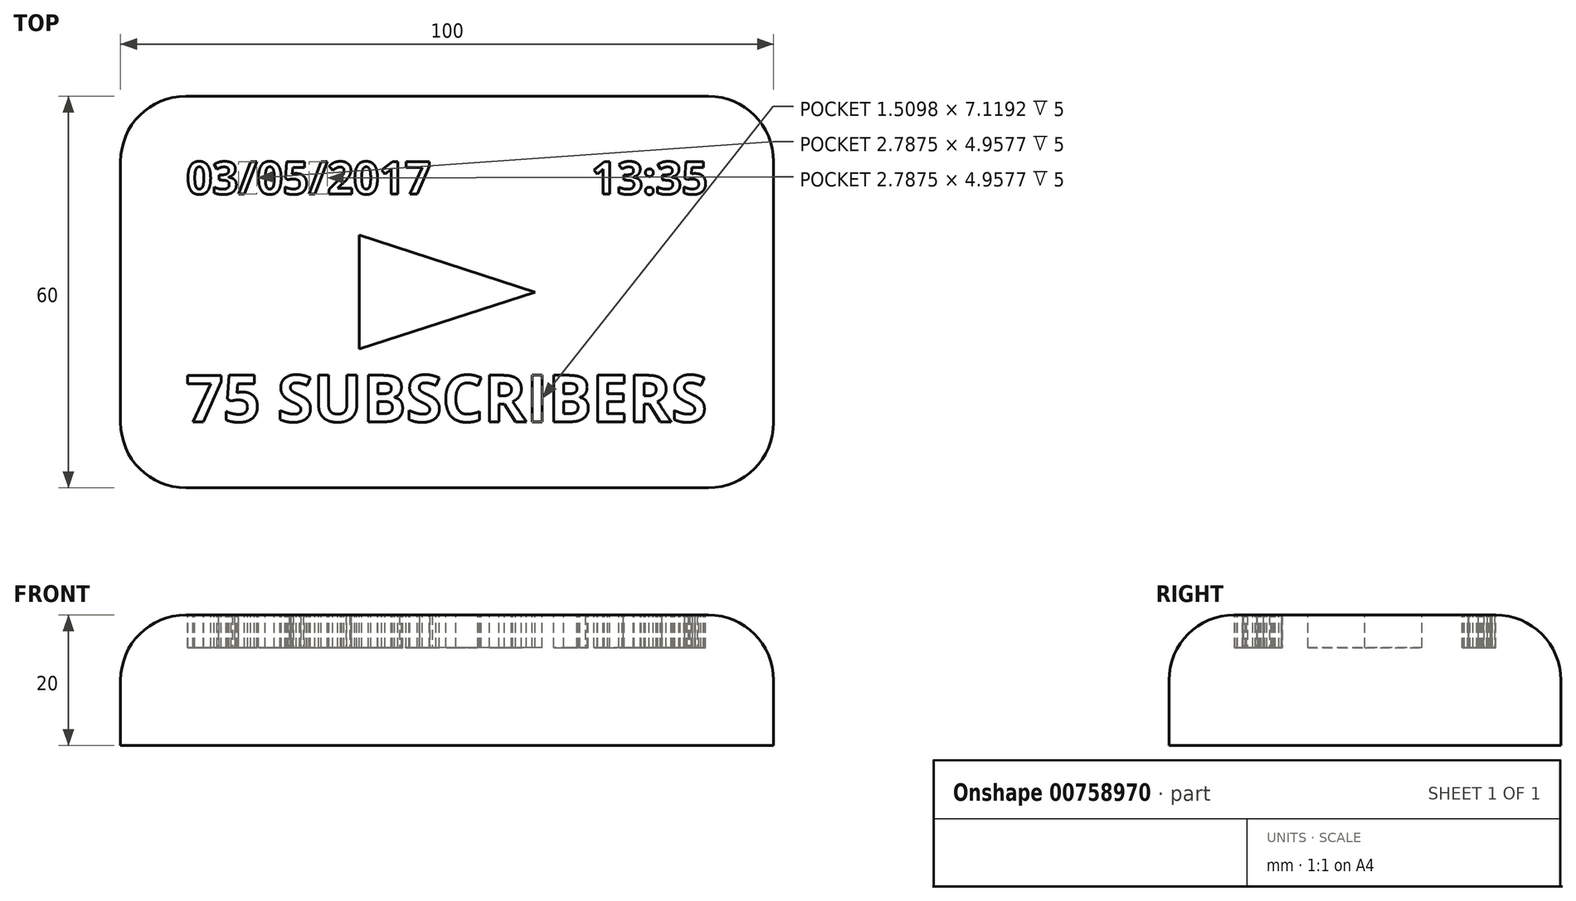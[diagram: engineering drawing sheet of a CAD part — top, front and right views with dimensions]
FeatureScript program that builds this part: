
annotation { "Feature Type Name" : "Feature", "Feature Type Description" : "" }
export const myFeature = defineFeature(function(context is Context, id is Id, definition is map)
    precondition{}
    {
        {
            var Q0;
            Q0=qCreatedBy(makeId("Top.planeOp"),FACE);
            var sketch = newSketch(context, id + "F0", { "sketchPlane" : qUnion([Q0])});
            skLineSegment(sketch, "E0.bottom", {"start": v(50, 30) * mm, "end": v(-50, 30) * mm});
            skLineSegment(sketch, "E0.top", {"start": v(50, -30) * mm, "end": v(-50, -30) * mm});
            skLineSegment(sketch, "E0.left", {"start": v(50, 30) * mm, "end": v(50, -30) * mm});
            skLineSegment(sketch, "E0.right", {"start": v(-50, 30) * mm, "end": v(-50, -30) * mm});
            skPoint(sketch, "E0.middle", {"position": v(0, 0) * mm});
            skSolve(sketch);
        }
        {
            var Q0;
            Q0=makeQuery(id+"F0.imprint","IMPRINT",FACE,{"disambiguationData":[TD([[makeQuery(id+"F0.imprint","IMPRINT",EDGE,{"derivedFrom":sQuery(id+"F0.wireOp",EDGE,"E0.bottom")}),1.0]])]});
            extrude(context, id + "F1", {"entities" : qUnion([Q0]), "depth" : 20 * mm, "offsetDistance" : 25 * mm});
        }
        {
            var Q0;
            Q0=makeQuery(id+"F1.opExtrude","CAP_FACE",FACE,{"disambiguationData":[OSD([sQuery(id+"F0.wireOp",EDGE,"E0.bottom"),sQuery(id+"F0.wireOp",EDGE,"E0.top"),sQuery(id+"F0.wireOp",EDGE,"E0.left"),sQuery(id+"F0.wireOp",EDGE,"E0.right")])],"isStart":false});
            var Q1;
            Q1=makeQuery(id+"F1.opExtrude","SWEPT_EDGE",EDGE,{"disambiguationData":[OSD([sQuery(id+"F0.wireOp",EDGE,"E0.top"),sQuery(id+"F0.wireOp",EDGE,"E0.left")])]});
            var Q2;
            Q2=makeQuery(id+"F1.opExtrude","SWEPT_EDGE",EDGE,{"disambiguationData":[OSD([sQuery(id+"F0.wireOp",EDGE,"E0.top"),sQuery(id+"F0.wireOp",EDGE,"E0.right")])]});
            var Q3;
            Q3=makeQuery(id+"F1.opExtrude","SWEPT_EDGE",EDGE,{"disambiguationData":[OSD([sQuery(id+"F0.wireOp",EDGE,"E0.bottom"),sQuery(id+"F0.wireOp",EDGE,"E0.right")])]});
            var Q4;
            Q4=makeQuery(id+"F1.opExtrude","SWEPT_EDGE",EDGE,{"disambiguationData":[OSD([sQuery(id+"F0.wireOp",EDGE,"E0.bottom"),sQuery(id+"F0.wireOp",EDGE,"E0.left")])]});
            fillet(context, id + "F2", {"entities" : qUnion([Q0, Q1, Q2, Q3, Q4]), "radius" : 10 * mm, "tangentPropagation" : true, "allowEdgeOverflow" : false});
        }
        {
            var Q0;
            Q0=makeQuery(id+"F1.opExtrude","CAP_FACE",FACE,{"disambiguationData":[OSD([sQuery(id+"F0.wireOp",EDGE,"E0.bottom"),sQuery(id+"F0.wireOp",EDGE,"E0.top"),sQuery(id+"F0.wireOp",EDGE,"E0.left"),sQuery(id+"F0.wireOp",EDGE,"E0.right")])],"isStart":false});
            var sketch = newSketch(context, id + "F4", { "sketchPlane" : qUnion([Q0])});
            skLineSegment(sketch, "E1.right", {"start": v(-13.45, 8.75) * mm, "end": v(-13.45, -8.75) * mm});
            skPoint(sketch, "E1.middle", {"position": v(0, 0) * mm});
            skLineSegment(sketch, "E2", {"start": v(-13.45, -8.75) * mm, "end": v(13.45, 0) * mm});
            skLineSegment(sketch, "E3", {"start": v(13.45, 0) * mm, "end": v(-13.45, 8.75) * mm});
            skSolve(sketch);
        }
        {
            var Q0;
            Q0=makeQuery(id+"F4.imprint","IMPRINT",FACE,{"disambiguationData":[TD([[makeQuery(id+"F4.imprint","IMPRINT",EDGE,{"derivedFrom":sQuery(id+"F4.wireOp",EDGE,"E1.right")}),-1.0]])]});
            var sketch = newSketch(context, id + "F5", { "sketchPlane" : qUnion([Q0])});
            skText(sketch, "E4", { "text": "75 SUBSCRIBERS", "fontName": "OpenSans-Bold.ttf"});
            skText(sketch, "E5", { "text": "03/05/2017", "fontName": "OpenSans-Bold.ttf"});
            skText(sketch, "E6", { "text": "13:35", "fontName": "OpenSans-Bold.ttf"});
            const initialGuessF5  = {"E4": [-0.03999, -0.01988, 1, 0, 0.00718], "E5": [-0.03993, 0.015, 1, 0, 0.005], "E6": [0.02206, 0.015, 1, 0, 0.005]};
            skSetInitialGuess(sketch, initialGuessF5);
            skSolve(sketch);
        }
        {
            var Q0;
            Q0=makeQuery(id+"F4.imprint","IMPRINT",FACE,{"disambiguationData":[TD([[makeQuery(id+"F4.imprint","IMPRINT",EDGE,{"derivedFrom":sQuery(id+"F4.wireOp",EDGE,"E1.right")}),1.0]])]});
            var Q1;
            Q1 = qSketchRegion(id + "F5", true);
            extrude(context, id + "F6", {"entities" : qUnion([Q0, Q1]), "operationType" : NewBodyOperationType.REMOVE, "oppositeDirection" : true, "depth" : 5 * mm, "offsetDistance" : 25 * mm});
        }
    });
